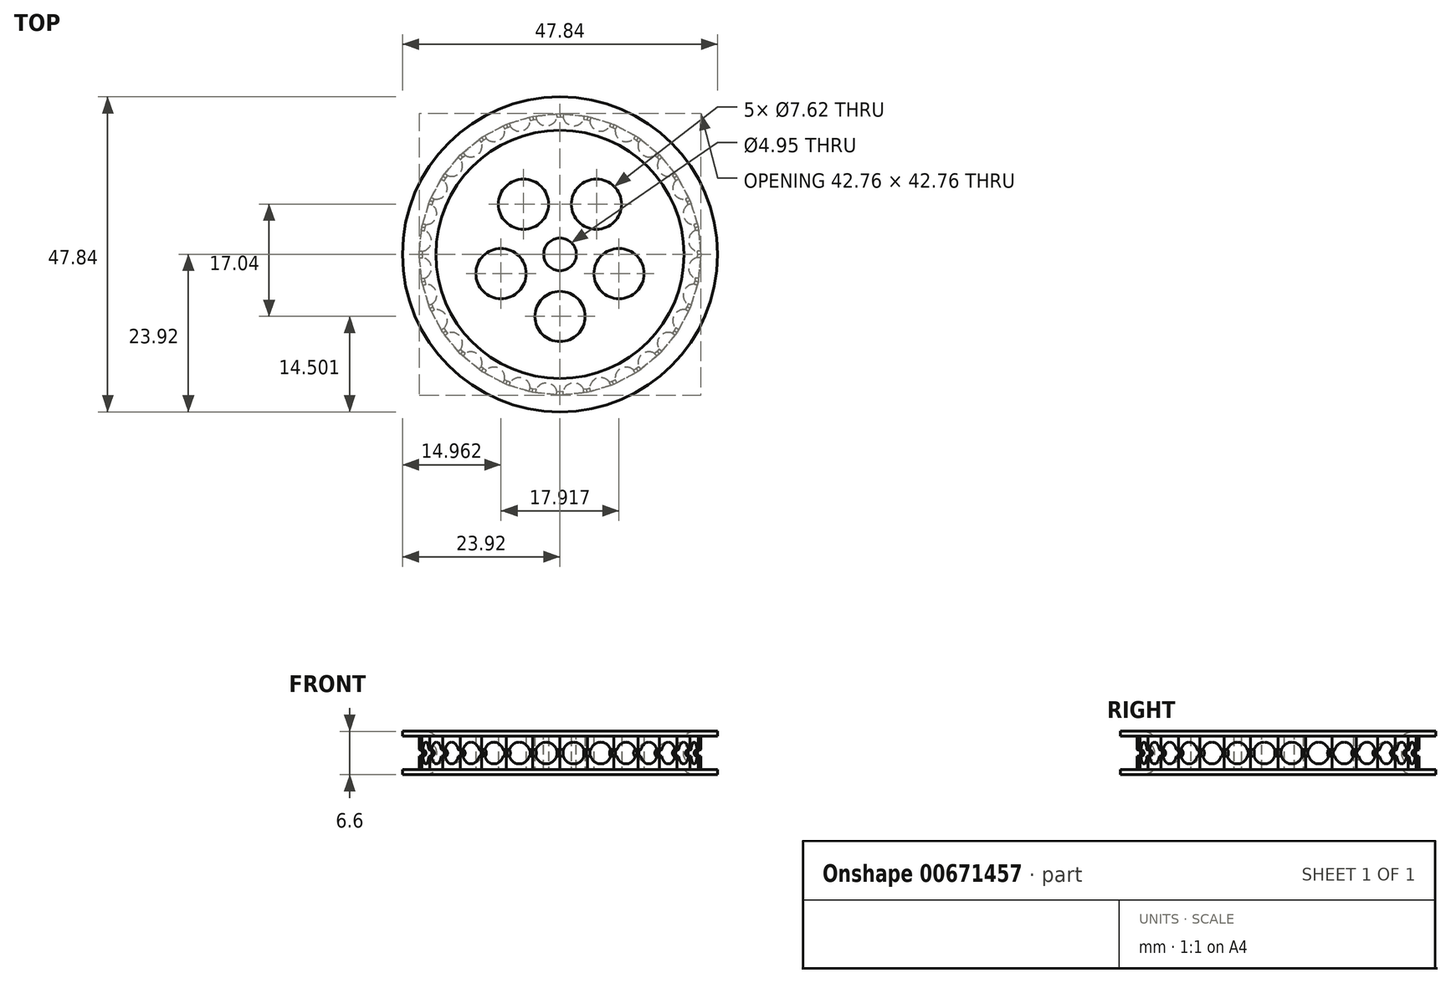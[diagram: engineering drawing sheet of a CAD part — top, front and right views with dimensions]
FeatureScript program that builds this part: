
annotation { "Feature Type Name" : "Feature", "Feature Type Description" : "" }
export const myFeature = defineFeature(function(context is Context, id is Id, definition is map)
    precondition{}
    {
        {
            var Q0;
            Q0=qCreatedBy(makeId("Top.planeOp"),FACE);
            var sketch = newSketch(context, id + "F0", { "sketchPlane" : qUnion([Q0])});
            skCircle(sketch, "E0.cCircle", {"center": v(0, 0) * mm, "radius": 21.38 * mm, "construction": true});
            skLineSegment(sketch, "E0.0", {"start": v(-21.38, 0) * mm, "end": v(-20.97, 4.17) * mm});
            skLineSegment(sketch, "E0.1", {"start": v(-20.97, 4.17) * mm, "end": v(-19.75, 8.18) * mm});
            skLineSegment(sketch, "E0.2", {"start": v(-19.75, 8.18) * mm, "end": v(-17.78, 11.88) * mm});
            skLineSegment(sketch, "E0.3", {"start": v(-17.78, 11.88) * mm, "end": v(-15.12, 15.12) * mm});
            skLineSegment(sketch, "E0.4", {"start": v(-15.12, 15.12) * mm, "end": v(-11.88, 17.78) * mm});
            skLineSegment(sketch, "E0.5", {"start": v(-11.88, 17.78) * mm, "end": v(-8.18, 19.75) * mm});
            skLineSegment(sketch, "E0.6", {"start": v(-8.18, 19.75) * mm, "end": v(-4.17, 20.97) * mm});
            skLineSegment(sketch, "E0.7", {"start": v(-4.17, 20.97) * mm, "end": v(0, 21.38) * mm});
            skLineSegment(sketch, "E0.8", {"start": v(0, 21.38) * mm, "end": v(4.17, 20.97) * mm});
            skLineSegment(sketch, "E0.9", {"start": v(4.17, 20.97) * mm, "end": v(8.18, 19.75) * mm});
            skLineSegment(sketch, "E0.10", {"start": v(8.18, 19.75) * mm, "end": v(11.88, 17.78) * mm});
            skLineSegment(sketch, "E0.11", {"start": v(11.88, 17.78) * mm, "end": v(15.12, 15.12) * mm});
            skLineSegment(sketch, "E0.12", {"start": v(15.12, 15.12) * mm, "end": v(17.78, 11.88) * mm});
            skLineSegment(sketch, "E0.13", {"start": v(17.78, 11.88) * mm, "end": v(19.75, 8.18) * mm});
            skLineSegment(sketch, "E0.14", {"start": v(19.75, 8.18) * mm, "end": v(20.97, 4.17) * mm});
            skLineSegment(sketch, "E0.15", {"start": v(20.97, 4.17) * mm, "end": v(21.38, 0) * mm});
            skLineSegment(sketch, "E0.16", {"start": v(21.38, 0) * mm, "end": v(20.97, -4.17) * mm});
            skLineSegment(sketch, "E0.17", {"start": v(20.97, -4.17) * mm, "end": v(19.75, -8.18) * mm});
            skLineSegment(sketch, "E0.18", {"start": v(19.75, -8.18) * mm, "end": v(17.78, -11.88) * mm});
            skLineSegment(sketch, "E0.19", {"start": v(17.78, -11.88) * mm, "end": v(15.12, -15.12) * mm});
            skLineSegment(sketch, "E0.20", {"start": v(15.12, -15.12) * mm, "end": v(11.88, -17.78) * mm});
            skLineSegment(sketch, "E0.21", {"start": v(11.88, -17.78) * mm, "end": v(8.18, -19.75) * mm});
            skLineSegment(sketch, "E0.22", {"start": v(8.18, -19.75) * mm, "end": v(4.17, -20.97) * mm});
            skLineSegment(sketch, "E0.23", {"start": v(4.17, -20.97) * mm, "end": v(0, -21.38) * mm});
            skLineSegment(sketch, "E0.24", {"start": v(0, -21.38) * mm, "end": v(-4.17, -20.97) * mm});
            skLineSegment(sketch, "E0.25", {"start": v(-4.17, -20.97) * mm, "end": v(-8.18, -19.75) * mm});
            skLineSegment(sketch, "E0.26", {"start": v(-8.18, -19.75) * mm, "end": v(-11.88, -17.78) * mm});
            skLineSegment(sketch, "E0.27", {"start": v(-11.88, -17.78) * mm, "end": v(-15.12, -15.12) * mm});
            skLineSegment(sketch, "E0.28", {"start": v(-15.12, -15.12) * mm, "end": v(-17.78, -11.88) * mm});
            skLineSegment(sketch, "E0.29", {"start": v(-17.78, -11.88) * mm, "end": v(-19.75, -8.18) * mm});
            skLineSegment(sketch, "E0.30", {"start": v(-19.75, -8.18) * mm, "end": v(-20.97, -4.17) * mm});
            skLineSegment(sketch, "E0.31", {"start": v(-20.97, -4.17) * mm, "end": v(-21.38, 0) * mm});
            skSolve(sketch);
        }
        {
            var Q0;
            Q0 = qSketchRegion(id + "F0", true);
            extrude(context, id + "F1", {"entities" : qUnion([Q0]), "endBound" : BoundingType.SYMMETRIC, "depth" : 5.08 * mm, "offsetDistance" : 25.4 * mm});
        }
        {
            var Q0;
            Q0=makeQuery(id+"F1.opExtrude","SWEPT_FACE",FACE,{"disambiguationData":[OSD([sQuery(id+"F0.wireOp",EDGE,"E0.28")])]});
            var sketch = newSketch(context, id + "F2", { "sketchPlane" : qUnion([Q0])});
            skLineSegment(sketch, "E1", {"start": v(2.1, 0) * mm, "end": v(-2.1, 0) * mm});
            skLineSegment(sketch, "E2", {"start": v(-2.1, 0) * mm, "end": v(-2.1, -0.5) * mm});
            skArc(sketch, "E3", {"start": v(-1.57, -0.5) * mm, "mid": v(0, -1.65) * mm, "end": v(1.57, -0.5) * mm});
            skLineSegment(sketch, "E4", {"start": v(-2.1, -0.5) * mm, "end": v(-1.57, -0.5) * mm});
            skPoint(sketch, "E5.orphan", {"position": v(-1.65, 0) * mm});
            skPoint(sketch, "E6.orphan", {"position": v(1.65, 0) * mm});
            skLineSegment(sketch, "E7", {"start": v(1.57, -0.5) * mm, "end": v(2.1, -0.5) * mm});
            skLineSegment(sketch, "E8", {"start": v(2.1, -0.5) * mm, "end": v(2.1, 0) * mm});
            skSolve(sketch);
        }
        {
            var Q0;
            Q0 = qSketchRegion(id + "F2", true);
            var Q1;
            Q1=sQuery(id+"F2.wireOp",EDGE,"E1");
            revolve(context, id + "F3", {"operationType" : NewBodyOperationType.REMOVE, "entities" : qUnion([Q0]), "axis" : qUnion([Q1]), "revolveType" : RevolveType.FULL, "oppositeDirection" : true});
        }
        {
            var Q0;
            Q0=makeQuery(id+"F1.opExtrude","SWEPT_FACE",FACE,{"disambiguationData":[OSD([sQuery(id+"F0.wireOp",EDGE,"E0.29")])]});
            var sketch = newSketch(context, id + "F4", { "sketchPlane" : qUnion([Q0])});
            skLineSegment(sketch, "E9", {"start": v(2.1, 0) * mm, "end": v(-2.1, 0) * mm});
            skPoint(sketch, "E9.startSnap0", {"position": v(-2.1, 0) * mm});
            skLineSegment(sketch, "E10", {"start": v(-2.1, 0) * mm, "end": v(-2.1, -0.5) * mm});
            skLineSegment(sketch, "E11", {"start": v(2.1, 0) * mm, "end": v(2.1, -0.5) * mm});
            skArc(sketch, "E12", {"start": v(-1.57, -0.5) * mm, "mid": v(0, -1.65) * mm, "end": v(1.57, -0.5) * mm});
            skLineSegment(sketch, "E13", {"start": v(-2.1, -0.5) * mm, "end": v(-1.57, -0.5) * mm});
            skLineSegment(sketch, "E14", {"start": v(1.57, -0.5) * mm, "end": v(2.1, -0.5) * mm});
            skPoint(sketch, "E15.orphan", {"position": v(-1.65, 0) * mm});
            skPoint(sketch, "E16.orphan", {"position": v(1.65, 0) * mm});
            skSolve(sketch);
        }
        {
            var Q0;
            Q0 = qSketchRegion(id + "F4", true);
            var Q1;
            Q1=sQuery(id+"F4.wireOp",EDGE,"E9");
            revolve(context, id + "F5", {"operationType" : NewBodyOperationType.REMOVE, "entities" : qUnion([Q0]), "axis" : qUnion([Q1]), "revolveType" : RevolveType.FULL, "oppositeDirection" : true});
        }
        {
            var Q0;
            Q0=makeQuery(id+"F1.opExtrude","SWEPT_FACE",FACE,{"disambiguationData":[OSD([sQuery(id+"F0.wireOp",EDGE,"E0.30")])]});
            var sketch = newSketch(context, id + "F6", { "sketchPlane" : qUnion([Q0])});
            skLineSegment(sketch, "E17", {"start": v(2.1, 0) * mm, "end": v(-2.1, 0) * mm});
            skLineSegment(sketch, "E18", {"start": v(-2.1, 0) * mm, "end": v(-2.1, -0.5) * mm});
            skLineSegment(sketch, "E19", {"start": v(2.1, 0) * mm, "end": v(2.1, -0.5) * mm});
            skArc(sketch, "E20", {"start": v(-1.57, -0.5) * mm, "mid": v(0, -1.65) * mm, "end": v(1.57, -0.5) * mm});
            skLineSegment(sketch, "E21", {"start": v(-2.1, -0.5) * mm, "end": v(-1.57, -0.5) * mm});
            skLineSegment(sketch, "E22", {"start": v(2.1, -0.5) * mm, "end": v(1.57, -0.5) * mm});
            skSolve(sketch);
        }
        {
            var Q0;
            Q0=makeQuery(id+"F6.imprint","IMPRINT",FACE,{"disambiguationData":[TD([[makeQuery(id+"F6.imprint","IMPRINT",EDGE,{"derivedFrom":sQuery(id+"F6.wireOp",EDGE,"E17")}),1.0]])]});
            var Q1;
            Q1=sQuery(id+"F6.wireOp",EDGE,"E17");
            revolve(context, id + "F7", {"operationType" : NewBodyOperationType.REMOVE, "entities" : qUnion([Q0]), "axis" : qUnion([Q1]), "revolveType" : RevolveType.FULL, "oppositeDirection" : true});
        }
        {
            var Q0;
            Q0=makeQuery(id+"F1.opExtrude","SWEPT_FACE",FACE,{"disambiguationData":[OSD([sQuery(id+"F0.wireOp",EDGE,"E0.31")])]});
            var sketch = newSketch(context, id + "F8", { "sketchPlane" : qUnion([Q0])});
            skLineSegment(sketch, "E23", {"start": v(2.1, 0) * mm, "end": v(-2.1, 0) * mm});
            skLineSegment(sketch, "E24", {"start": v(-2.1, -0.5) * mm, "end": v(-2.1, 0) * mm});
            skLineSegment(sketch, "E25", {"start": v(2.1, -0.5) * mm, "end": v(2.1, 0) * mm});
            skArc(sketch, "E26", {"start": v(-1.57, -0.5) * mm, "mid": v(0, -1.65) * mm, "end": v(1.57, -0.5) * mm});
            skLineSegment(sketch, "E27", {"start": v(-2.1, -0.5) * mm, "end": v(-1.57, -0.5) * mm});
            skLineSegment(sketch, "E28", {"start": v(2.1, -0.5) * mm, "end": v(1.57, -0.5) * mm});
            skSolve(sketch);
        }
        {
            var Q0;
            Q0 = qSketchRegion(id + "F8", true);
            var Q1;
            Q1=sQuery(id+"F8.wireOp",EDGE,"E23");
            revolve(context, id + "F9", {"operationType" : NewBodyOperationType.REMOVE, "entities" : qUnion([Q0]), "axis" : qUnion([Q1]), "revolveType" : RevolveType.FULL, "oppositeDirection" : true});
        }
        {
            var Q0;
            Q0=makeQuery(id+"F1.opExtrude","SWEPT_FACE",FACE,{"disambiguationData":[OSD([sQuery(id+"F0.wireOp",EDGE,"E0.0")])]});
            var sketch = newSketch(context, id + "F10", { "sketchPlane" : qUnion([Q0])});
            skLineSegment(sketch, "E29", {"start": v(2.1, 0) * mm, "end": v(-2.1, 0) * mm});
            skArc(sketch, "E30", {"start": v(-1.57, -0.5) * mm, "mid": v(0, -1.65) * mm, "end": v(1.57, -0.5) * mm});
            skLineSegment(sketch, "E31", {"start": v(2.1, -0.5) * mm, "end": v(1.57, -0.5) * mm});
            skLineSegment(sketch, "E32", {"start": v(2.1, -0.5) * mm, "end": v(2.1, 0) * mm});
            skLineSegment(sketch, "E33", {"start": v(-1.57, -0.5) * mm, "end": v(-2.1, -0.5) * mm});
            skLineSegment(sketch, "E34", {"start": v(-2.1, -0.5) * mm, "end": v(-2.1, 0) * mm});
            skSolve(sketch);
        }
        {
            var Q0;
            Q0 = qSketchRegion(id + "F10", true);
            var Q1;
            Q1=sQuery(id+"F10.wireOp",EDGE,"E29");
            revolve(context, id + "F11", {"operationType" : NewBodyOperationType.REMOVE, "entities" : qUnion([Q0]), "axis" : qUnion([Q1]), "revolveType" : RevolveType.FULL, "oppositeDirection" : true});
        }
        {
            var Q0;
            Q0=makeQuery(id+"F1.opExtrude","SWEPT_FACE",FACE,{"disambiguationData":[OSD([sQuery(id+"F0.wireOp",EDGE,"E0.1")])]});
            var sketch = newSketch(context, id + "F12", { "sketchPlane" : qUnion([Q0])});
            skLineSegment(sketch, "E35", {"start": v(2.1, 0) * mm, "end": v(-2.1, 0) * mm});
            skArc(sketch, "E36", {"start": v(-1.57, -0.5) * mm, "mid": v(0, -1.65) * mm, "end": v(1.57, -0.5) * mm});
            skLineSegment(sketch, "E37", {"start": v(2.1, -0.5) * mm, "end": v(1.57, -0.5) * mm});
            skLineSegment(sketch, "E38", {"start": v(1.57, -0.5) * mm, "end": v(2.1, -0.5) * mm});
            skLineSegment(sketch, "E39", {"start": v(2.1, 0) * mm, "end": v(2.1, -0.5) * mm});
            skLineSegment(sketch, "E40", {"start": v(-2.1, 0) * mm, "end": v(-2.1, -0.5) * mm});
            skLineSegment(sketch, "E41", {"start": v(-2.1, -0.5) * mm, "end": v(-1.57, -0.5) * mm});
            skSolve(sketch);
        }
        {
            var Q0;
            Q0 = qSketchRegion(id + "F12", true);
            var Q1;
            Q1=sQuery(id+"F12.wireOp",EDGE,"E35");
            revolve(context, id + "F13", {"operationType" : NewBodyOperationType.REMOVE, "entities" : qUnion([Q0]), "axis" : qUnion([Q1]), "revolveType" : RevolveType.FULL, "oppositeDirection" : true});
        }
        {
            var Q0;
            Q0=makeQuery(id+"F1.opExtrude","SWEPT_FACE",FACE,{"disambiguationData":[OSD([sQuery(id+"F0.wireOp",EDGE,"E0.2")])]});
            var sketch = newSketch(context, id + "F14", { "sketchPlane" : qUnion([Q0])});
            skLineSegment(sketch, "E42", {"start": v(2.1, 0) * mm, "end": v(-2.1, 0) * mm});
            skArc(sketch, "E43", {"start": v(-1.57, -0.5) * mm, "mid": v(0, -1.65) * mm, "end": v(1.57, -0.5) * mm});
            skLineSegment(sketch, "E44", {"start": v(2.1, -0.5) * mm, "end": v(1.57, -0.5) * mm});
            skLineSegment(sketch, "E45", {"start": v(-1.57, -0.5) * mm, "end": v(-2.1, -0.5) * mm});
            skLineSegment(sketch, "E46", {"start": v(-2.1, -0.5) * mm, "end": v(-2.1, 0) * mm});
            skLineSegment(sketch, "E47", {"start": v(2.1, -0.5) * mm, "end": v(2.1, 0) * mm});
            skSolve(sketch);
        }
        {
            var Q0;
            Q0 = qSketchRegion(id + "F14", true);
            var Q1;
            Q1=sQuery(id+"F14.wireOp",EDGE,"E42");
            revolve(context, id + "F15", {"operationType" : NewBodyOperationType.REMOVE, "entities" : qUnion([Q0]), "axis" : qUnion([Q1]), "revolveType" : RevolveType.FULL, "oppositeDirection" : true});
        }
        {
            var Q0;
            Q0=makeQuery(id+"F1.opExtrude","SWEPT_FACE",FACE,{"disambiguationData":[OSD([sQuery(id+"F0.wireOp",EDGE,"E0.3")])]});
            var sketch = newSketch(context, id + "F16", { "sketchPlane" : qUnion([Q0])});
            skLineSegment(sketch, "E48", {"start": v(2.1, 0) * mm, "end": v(-2.1, 0) * mm});
            skArc(sketch, "E49", {"start": v(-1.57, -0.5) * mm, "mid": v(0, -1.65) * mm, "end": v(1.57, -0.5) * mm});
            skLineSegment(sketch, "E50", {"start": v(2.1, -0.5) * mm, "end": v(1.57, -0.5) * mm});
            skLineSegment(sketch, "E51", {"start": v(-1.57, -0.5) * mm, "end": v(-2.1, -0.5) * mm});
            skLineSegment(sketch, "E52", {"start": v(-2.1, -0.5) * mm, "end": v(-2.1, 0) * mm});
            skLineSegment(sketch, "E53", {"start": v(2.1, -0.5) * mm, "end": v(2.1, 0) * mm});
            skSolve(sketch);
        }
        {
            var Q0;
            Q0 = qSketchRegion(id + "F16", true);
            var Q1;
            Q1=sQuery(id+"F16.wireOp",EDGE,"E48");
            revolve(context, id + "F17", {"operationType" : NewBodyOperationType.REMOVE, "entities" : qUnion([Q0]), "axis" : qUnion([Q1]), "revolveType" : RevolveType.FULL, "oppositeDirection" : true});
        }
        {
            var Q0;
            Q0=makeQuery(id+"F1.opExtrude","SWEPT_FACE",FACE,{"disambiguationData":[OSD([sQuery(id+"F0.wireOp",EDGE,"E0.4")])]});
            var sketch = newSketch(context, id + "F18", { "sketchPlane" : qUnion([Q0])});
            skLineSegment(sketch, "E54", {"start": v(2.1, 0) * mm, "end": v(-2.1, 0) * mm});
            skArc(sketch, "E55", {"start": v(-1.57, -0.5) * mm, "mid": v(0, -1.65) * mm, "end": v(1.57, -0.5) * mm});
            skLineSegment(sketch, "E56", {"start": v(2.1, -0.5) * mm, "end": v(1.57, -0.5) * mm});
            skLineSegment(sketch, "E57", {"start": v(2.1, 0) * mm, "end": v(2.1, -0.5) * mm});
            skLineSegment(sketch, "E58", {"start": v(-2.1, 0) * mm, "end": v(-2.1, -0.5) * mm});
            skLineSegment(sketch, "E59", {"start": v(-2.1, -0.5) * mm, "end": v(-1.57, -0.5) * mm});
            skSolve(sketch);
        }
        {
            var Q0;
            Q0 = qSketchRegion(id + "F18", true);
            var Q1;
            Q1=sQuery(id+"F18.wireOp",EDGE,"E54");
            revolve(context, id + "F19", {"operationType" : NewBodyOperationType.REMOVE, "entities" : qUnion([Q0]), "axis" : qUnion([Q1]), "revolveType" : RevolveType.FULL, "oppositeDirection" : true});
        }
        {
            var Q0;
            Q0=makeQuery(id+"F1.opExtrude","SWEPT_FACE",FACE,{"disambiguationData":[OSD([sQuery(id+"F0.wireOp",EDGE,"E0.5")])]});
            var sketch = newSketch(context, id + "F20", { "sketchPlane" : qUnion([Q0])});
            skLineSegment(sketch, "E60", {"start": v(2.1, 0) * mm, "end": v(-2.1, 0) * mm});
            skLineSegment(sketch, "E61", {"start": v(-2.1, 0) * mm, "end": v(-2.1, -0.5) * mm});
            skLineSegment(sketch, "E62", {"start": v(2.1, 0) * mm, "end": v(2.1, -0.5) * mm});
            skLineSegment(sketch, "E63", {"start": v(-2.1, -0.5) * mm, "end": v(-1.57, -0.5) * mm});
            skArc(sketch, "E64", {"start": v(-1.57, -0.5) * mm, "mid": v(0, -1.65) * mm, "end": v(1.57, -0.5) * mm});
            skLineSegment(sketch, "E65.trimOffspring", {"start": v(1.57, -0.5) * mm, "end": v(2.1, -0.5) * mm});
            skSolve(sketch);
        }
        {
            var Q0;
            Q0 = qSketchRegion(id + "F20", true);
            var Q1;
            Q1=sQuery(id+"F20.wireOp",EDGE,"E60");
            revolve(context, id + "F21", {"operationType" : NewBodyOperationType.REMOVE, "entities" : qUnion([Q0]), "axis" : qUnion([Q1]), "revolveType" : RevolveType.FULL, "oppositeDirection" : true});
        }
        {
            var Q0;
            Q0=makeQuery(id+"F1.opExtrude","SWEPT_FACE",FACE,{"disambiguationData":[OSD([sQuery(id+"F0.wireOp",EDGE,"E0.6")])]});
            var sketch = newSketch(context, id + "F22", { "sketchPlane" : qUnion([Q0])});
            skLineSegment(sketch, "E66", {"start": v(2.1, 0) * mm, "end": v(-2.1, 0) * mm});
            skLineSegment(sketch, "E67", {"start": v(-2.1, 0) * mm, "end": v(-2.1, -0.5) * mm});
            skLineSegment(sketch, "E68", {"start": v(-2.1, -0.5) * mm, "end": v(-1.57, -0.5) * mm});
            skLineSegment(sketch, "E69", {"start": v(2.1, -0.5) * mm, "end": v(2.1, 0) * mm});
            skArc(sketch, "E70", {"start": v(-1.57, -0.5) * mm, "mid": v(0, -1.65) * mm, "end": v(1.57, -0.5) * mm});
            skLineSegment(sketch, "E71.trimOffspring", {"start": v(1.57, -0.5) * mm, "end": v(2.1, -0.5) * mm});
            skSolve(sketch);
        }
        {
            var Q0;
            Q0 = qSketchRegion(id + "F22", true);
            var Q1;
            Q1=sQuery(id+"F22.wireOp",EDGE,"E66");
            revolve(context, id + "F23", {"operationType" : NewBodyOperationType.REMOVE, "entities" : qUnion([Q0]), "axis" : qUnion([Q1]), "revolveType" : RevolveType.FULL, "oppositeDirection" : true});
        }
        {
            var Q0;
            Q0=makeQuery(id+"F1.opExtrude","SWEPT_FACE",FACE,{"disambiguationData":[OSD([sQuery(id+"F0.wireOp",EDGE,"E0.7")])]});
            var sketch = newSketch(context, id + "F24", { "sketchPlane" : qUnion([Q0])});
            skLineSegment(sketch, "E72", {"start": v(2.1, 0) * mm, "end": v(-2.1, 0) * mm});
            skLineSegment(sketch, "E73", {"start": v(-2.1, 0) * mm, "end": v(-2.1, -0.5) * mm});
            skLineSegment(sketch, "E74", {"start": v(-2.1, -0.5) * mm, "end": v(-1.57, -0.5) * mm});
            skLineSegment(sketch, "E75", {"start": v(2.1, -0.5) * mm, "end": v(2.1, 0) * mm});
            skArc(sketch, "E76", {"start": v(-1.57, -0.5) * mm, "mid": v(0, -1.65) * mm, "end": v(1.57, -0.5) * mm});
            skLineSegment(sketch, "E77.trimOffspring", {"start": v(1.57, -0.5) * mm, "end": v(2.1, -0.5) * mm});
            skSolve(sketch);
        }
        {
            var Q0;
            Q0 = qSketchRegion(id + "F24", true);
            var Q1;
            Q1=sQuery(id+"F24.wireOp",EDGE,"E72");
            revolve(context, id + "F25", {"operationType" : NewBodyOperationType.REMOVE, "entities" : qUnion([Q0]), "axis" : qUnion([Q1]), "revolveType" : RevolveType.FULL, "oppositeDirection" : true});
        }
        {
            var Q0;
            Q0=makeQuery(id+"F1.opExtrude","SWEPT_FACE",FACE,{"disambiguationData":[OSD([sQuery(id+"F0.wireOp",EDGE,"E0.8")])]});
            var sketch = newSketch(context, id + "F26", { "sketchPlane" : qUnion([Q0])});
            skLineSegment(sketch, "E78", {"start": v(2.1, 0) * mm, "end": v(-2.1, 0) * mm});
            skLineSegment(sketch, "E79", {"start": v(-2.1, 0) * mm, "end": v(-2.1, -0.5) * mm});
            skLineSegment(sketch, "E80", {"start": v(-2.1, -0.5) * mm, "end": v(-1.57, -0.5) * mm});
            skLineSegment(sketch, "E81", {"start": v(2.1, -0.5) * mm, "end": v(2.1, 0) * mm});
            skArc(sketch, "E82", {"start": v(-1.57, -0.5) * mm, "mid": v(0, -1.65) * mm, "end": v(1.57, -0.5) * mm});
            skLineSegment(sketch, "E83.trimOffspring", {"start": v(1.57, -0.5) * mm, "end": v(2.1, -0.5) * mm});
            skSolve(sketch);
        }
        {
            var Q0;
            Q0 = qSketchRegion(id + "F26", true);
            var Q1;
            Q1=sQuery(id+"F26.wireOp",EDGE,"E78");
            revolve(context, id + "F27", {"operationType" : NewBodyOperationType.REMOVE, "entities" : qUnion([Q0]), "axis" : qUnion([Q1]), "revolveType" : RevolveType.FULL, "oppositeDirection" : true});
        }
        {
            var Q0;
            Q0=makeQuery(id+"F1.opExtrude","SWEPT_FACE",FACE,{"disambiguationData":[OSD([sQuery(id+"F0.wireOp",EDGE,"E0.9")])]});
            var sketch = newSketch(context, id + "F28", { "sketchPlane" : qUnion([Q0])});
            skLineSegment(sketch, "E84", {"start": v(2.1, 0) * mm, "end": v(-2.1, 0) * mm});
            skLineSegment(sketch, "E85", {"start": v(-2.1, 0) * mm, "end": v(-2.1, -0.5) * mm});
            skLineSegment(sketch, "E86", {"start": v(2.1, -0.5) * mm, "end": v(1.57, -0.5) * mm});
            skLineSegment(sketch, "E87", {"start": v(2.1, -0.5) * mm, "end": v(2.1, 0) * mm});
            skArc(sketch, "E88", {"start": v(-1.57, -0.5) * mm, "mid": v(0, -1.65) * mm, "end": v(1.57, -0.5) * mm});
            skLineSegment(sketch, "E89.trimOffspring", {"start": v(-1.57, -0.5) * mm, "end": v(-2.1, -0.5) * mm});
            skSolve(sketch);
        }
        {
            var Q0;
            Q0 = qSketchRegion(id + "F28", true);
            var Q1;
            Q1=sQuery(id+"F28.wireOp",EDGE,"E84");
            revolve(context, id + "F29", {"operationType" : NewBodyOperationType.REMOVE, "entities" : qUnion([Q0]), "axis" : qUnion([Q1]), "revolveType" : RevolveType.FULL, "oppositeDirection" : true});
        }
        {
            var Q0;
            Q0=makeQuery(id+"F1.opExtrude","SWEPT_FACE",FACE,{"disambiguationData":[OSD([sQuery(id+"F0.wireOp",EDGE,"E0.10")])]});
            var sketch = newSketch(context, id + "F30", { "sketchPlane" : qUnion([Q0])});
            skLineSegment(sketch, "E90", {"start": v(2.1, 0) * mm, "end": v(-2.1, 0) * mm});
            skLineSegment(sketch, "E91", {"start": v(-2.1, 0) * mm, "end": v(-2.1, -0.5) * mm});
            skLineSegment(sketch, "E92", {"start": v(-2.1, -0.5) * mm, "end": v(-1.57, -0.5) * mm});
            skLineSegment(sketch, "E93", {"start": v(2.1, 0) * mm, "end": v(2.1, -0.5) * mm});
            skArc(sketch, "E94", {"start": v(-1.57, -0.5) * mm, "mid": v(0, -1.65) * mm, "end": v(1.57, -0.5) * mm});
            skLineSegment(sketch, "E95.trimOffspring", {"start": v(1.57, -0.5) * mm, "end": v(2.1, -0.5) * mm});
            skSolve(sketch);
        }
        {
            var Q0;
            Q0 = qSketchRegion(id + "F30", true);
            var Q1;
            Q1=sQuery(id+"F30.wireOp",EDGE,"E90");
            revolve(context, id + "F31", {"operationType" : NewBodyOperationType.REMOVE, "entities" : qUnion([Q0]), "axis" : qUnion([Q1]), "revolveType" : RevolveType.FULL, "oppositeDirection" : true});
        }
        {
            var Q0;
            Q0=makeQuery(id+"F1.opExtrude","SWEPT_FACE",FACE,{"disambiguationData":[OSD([sQuery(id+"F0.wireOp",EDGE,"E0.11")])]});
            var sketch = newSketch(context, id + "F32", { "sketchPlane" : qUnion([Q0])});
            skLineSegment(sketch, "E96", {"start": v(2.1, 0) * mm, "end": v(-2.1, 0) * mm});
            skLineSegment(sketch, "E97", {"start": v(-2.1, 0) * mm, "end": v(-2.1, -0.5) * mm});
            skLineSegment(sketch, "E98", {"start": v(-2.1, -0.5) * mm, "end": v(-1.57, -0.5) * mm});
            skLineSegment(sketch, "E99", {"start": v(2.1, -0.5) * mm, "end": v(2.1, 0) * mm});
            skArc(sketch, "E100", {"start": v(-1.57, -0.5) * mm, "mid": v(0, -1.65) * mm, "end": v(1.57, -0.5) * mm});
            skLineSegment(sketch, "E101.trimOffspring", {"start": v(1.57, -0.5) * mm, "end": v(2.1, -0.5) * mm});
            skSolve(sketch);
        }
        {
            var Q0;
            Q0 = qSketchRegion(id + "F32", true);
            var Q1;
            Q1=sQuery(id+"F32.wireOp",EDGE,"E96");
            revolve(context, id + "F33", {"operationType" : NewBodyOperationType.REMOVE, "entities" : qUnion([Q0]), "axis" : qUnion([Q1]), "revolveType" : RevolveType.FULL, "oppositeDirection" : true});
        }
        {
            var Q0;
            Q0=makeQuery(id+"F1.opExtrude","SWEPT_FACE",FACE,{"disambiguationData":[OSD([sQuery(id+"F0.wireOp",EDGE,"E0.12")])]});
            var sketch = newSketch(context, id + "F34", { "sketchPlane" : qUnion([Q0])});
            skLineSegment(sketch, "E102", {"start": v(2.1, 0) * mm, "end": v(-2.1, 0) * mm});
            skLineSegment(sketch, "E103", {"start": v(-2.1, 0) * mm, "end": v(-2.1, -0.5) * mm});
            skLineSegment(sketch, "E104", {"start": v(-2.1, -0.5) * mm, "end": v(-1.57, -0.5) * mm});
            skArc(sketch, "E105", {"start": v(-1.57, -0.5) * mm, "mid": v(0, -1.65) * mm, "end": v(1.57, -0.5) * mm});
            skLineSegment(sketch, "E106.trimOffspring", {"start": v(1.57, -0.5) * mm, "end": v(2.1, -0.5) * mm});
            skSolve(sketch);
        }
        {
            var Q0;
            {var subQ0=sQuery(id+"F34.wireOp",EDGE,"E102");Q0=makeQuery(id+"F34.imprint","IMPRINT",FACE,{"disambiguationData":[TD([[makeQuery(id+"F34.imprint","IMPRINT",EDGE,{"derivedFrom":subQ0}),1.0]])]});}
            var Q1;
            Q1=sQuery(id+"F34.wireOp",EDGE,"E102");
            revolve(context, id + "F35", {"operationType" : NewBodyOperationType.REMOVE, "entities" : qUnion([Q0]), "axis" : qUnion([Q1]), "revolveType" : RevolveType.FULL, "oppositeDirection" : true});
        }
        {
            var Q0;
            Q0=makeQuery(id+"F1.opExtrude","SWEPT_FACE",FACE,{"disambiguationData":[OSD([sQuery(id+"F0.wireOp",EDGE,"E0.13")])]});
            var sketch = newSketch(context, id + "F36", { "sketchPlane" : qUnion([Q0])});
            skLineSegment(sketch, "E107", {"start": v(2.1, 0) * mm, "end": v(-2.1, 0) * mm});
            skLineSegment(sketch, "E108", {"start": v(-2.1, -0.5) * mm, "end": v(-2.1, 0) * mm});
            skLineSegment(sketch, "E109", {"start": v(-2.1, -0.5) * mm, "end": v(-1.57, -0.5) * mm});
            skLineSegment(sketch, "E110", {"start": v(2.1, 0) * mm, "end": v(2.1, -0.5) * mm});
            skArc(sketch, "E111", {"start": v(-1.57, -0.5) * mm, "mid": v(0, -1.65) * mm, "end": v(1.57, -0.5) * mm});
            skLineSegment(sketch, "E112.trimOffspring", {"start": v(1.57, -0.5) * mm, "end": v(2.1, -0.5) * mm});
            skSolve(sketch);
        }
        {
            var Q0;
            Q0 = qSketchRegion(id + "F36", true);
            var Q1;
            Q1=sQuery(id+"F36.wireOp",EDGE,"E107");
            revolve(context, id + "F37", {"operationType" : NewBodyOperationType.REMOVE, "entities" : qUnion([Q0]), "axis" : qUnion([Q1]), "revolveType" : RevolveType.FULL, "oppositeDirection" : true});
        }
        {
            var Q0;
            Q0=makeQuery(id+"F1.opExtrude","SWEPT_FACE",FACE,{"disambiguationData":[OSD([sQuery(id+"F0.wireOp",EDGE,"E0.14")])]});
            var sketch = newSketch(context, id + "F38", { "sketchPlane" : qUnion([Q0])});
            skLineSegment(sketch, "E113", {"start": v(2.1, 0) * mm, "end": v(-2.1, 0) * mm});
            skLineSegment(sketch, "E114", {"start": v(-2.1, 0) * mm, "end": v(-2.1, -0.5) * mm});
            skLineSegment(sketch, "E115", {"start": v(-2.1, -0.5) * mm, "end": v(-1.57, -0.5) * mm});
            skLineSegment(sketch, "E116", {"start": v(2.1, -0.5) * mm, "end": v(2.1, 0) * mm});
            skArc(sketch, "E117", {"start": v(-1.57, -0.5) * mm, "mid": v(0, -1.65) * mm, "end": v(1.57, -0.5) * mm});
            skLineSegment(sketch, "E118.trimOffspring", {"start": v(1.57, -0.5) * mm, "end": v(2.1, -0.5) * mm});
            skSolve(sketch);
        }
        {
            var Q0;
            Q0 = qSketchRegion(id + "F38", true);
            var Q1;
            Q1=sQuery(id+"F38.wireOp",EDGE,"E113");
            revolve(context, id + "F39", {"operationType" : NewBodyOperationType.REMOVE, "entities" : qUnion([Q0]), "axis" : qUnion([Q1]), "revolveType" : RevolveType.FULL, "oppositeDirection" : true});
        }
        {
            var Q0;
            Q0=makeQuery(id+"F1.opExtrude","SWEPT_FACE",FACE,{"disambiguationData":[OSD([sQuery(id+"F0.wireOp",EDGE,"E0.15")])]});
            var sketch = newSketch(context, id + "F40", { "sketchPlane" : qUnion([Q0])});
            skLineSegment(sketch, "E119", {"start": v(2.1, 0) * mm, "end": v(-2.1, 0) * mm});
            skLineSegment(sketch, "E120", {"start": v(-2.1, 0) * mm, "end": v(-2.1, -0.5) * mm});
            skLineSegment(sketch, "E121", {"start": v(-2.1, -0.5) * mm, "end": v(-1.57, -0.5) * mm});
            skLineSegment(sketch, "E122", {"start": v(2.1, 0) * mm, "end": v(2.1, -0.5) * mm});
            skArc(sketch, "E123", {"start": v(-1.57, -0.5) * mm, "mid": v(0, -1.65) * mm, "end": v(1.57, -0.5) * mm});
            skLineSegment(sketch, "E124.trimOffspring", {"start": v(1.57, -0.5) * mm, "end": v(2.1, -0.5) * mm});
            skSolve(sketch);
        }
        {
            var Q0;
            Q0 = qSketchRegion(id + "F40", true);
            var Q1;
            Q1=sQuery(id+"F40.wireOp",EDGE,"E119");
            revolve(context, id + "F41", {"operationType" : NewBodyOperationType.REMOVE, "entities" : qUnion([Q0]), "axis" : qUnion([Q1]), "revolveType" : RevolveType.FULL, "oppositeDirection" : true});
        }
        {
            var Q0;
            Q0=makeQuery(id+"F1.opExtrude","SWEPT_FACE",FACE,{"disambiguationData":[OSD([sQuery(id+"F0.wireOp",EDGE,"E0.16")])]});
            var sketch = newSketch(context, id + "F42", { "sketchPlane" : qUnion([Q0])});
            skLineSegment(sketch, "E125", {"start": v(2.1, 0) * mm, "end": v(-2.1, 0) * mm});
            skLineSegment(sketch, "E126", {"start": v(-2.1, 0) * mm, "end": v(-2.1, -0.5) * mm});
            skLineSegment(sketch, "E127", {"start": v(2.1, 0) * mm, "end": v(2.1, -0.5) * mm});
            skLineSegment(sketch, "E128", {"start": v(2.1, -0.5) * mm, "end": v(1.57, -0.5) * mm});
            skArc(sketch, "E129", {"start": v(-1.57, -0.5) * mm, "mid": v(0, -1.65) * mm, "end": v(1.57, -0.5) * mm});
            skLineSegment(sketch, "E130.trimOffspring", {"start": v(-1.57, -0.5) * mm, "end": v(-2.1, -0.5) * mm});
            skSolve(sketch);
        }
        {
            var Q0;
            Q0 = qSketchRegion(id + "F42", true);
            var Q1;
            Q1=sQuery(id+"F42.wireOp",EDGE,"E125");
            revolve(context, id + "F43", {"operationType" : NewBodyOperationType.REMOVE, "entities" : qUnion([Q0]), "axis" : qUnion([Q1]), "revolveType" : RevolveType.FULL, "oppositeDirection" : true});
        }
        {
            var Q0;
            Q0=makeQuery(id+"F1.opExtrude","SWEPT_FACE",FACE,{"disambiguationData":[OSD([sQuery(id+"F0.wireOp",EDGE,"E0.17")])]});
            var sketch = newSketch(context, id + "F44", { "sketchPlane" : qUnion([Q0])});
            skLineSegment(sketch, "E131", {"start": v(2.1, 0) * mm, "end": v(-2.1, 0) * mm});
            skLineSegment(sketch, "E132", {"start": v(-2.1, -0.5) * mm, "end": v(-2.1, 0) * mm});
            skLineSegment(sketch, "E133", {"start": v(-2.1, -0.5) * mm, "end": v(-1.57, -0.5) * mm});
            skLineSegment(sketch, "E134", {"start": v(2.1, -0.5) * mm, "end": v(2.1, 0) * mm});
            skArc(sketch, "E135", {"start": v(-1.57, -0.5) * mm, "mid": v(0, -1.65) * mm, "end": v(1.57, -0.5) * mm});
            skLineSegment(sketch, "E136.trimOffspring", {"start": v(1.57, -0.5) * mm, "end": v(2.1, -0.5) * mm});
            skSolve(sketch);
        }
        {
            var Q0;
            Q0 = qSketchRegion(id + "F44", true);
            var Q1;
            Q1=sQuery(id+"F44.wireOp",EDGE,"E131");
            revolve(context, id + "F45", {"operationType" : NewBodyOperationType.REMOVE, "entities" : qUnion([Q0]), "axis" : qUnion([Q1]), "revolveType" : RevolveType.FULL, "oppositeDirection" : true});
        }
        {
            var Q0;
            Q0=makeQuery(id+"F1.opExtrude","SWEPT_FACE",FACE,{"disambiguationData":[OSD([sQuery(id+"F0.wireOp",EDGE,"E0.18")])]});
            var sketch = newSketch(context, id + "F46", { "sketchPlane" : qUnion([Q0])});
            skLineSegment(sketch, "E137", {"start": v(2.1, 0) * mm, "end": v(-2.1, 0) * mm});
            skLineSegment(sketch, "E138", {"start": v(-2.1, 0) * mm, "end": v(-2.1, -0.5) * mm});
            skLineSegment(sketch, "E139", {"start": v(-2.1, -0.5) * mm, "end": v(-1.57, -0.5) * mm});
            skLineSegment(sketch, "E140", {"start": v(2.1, -0.5) * mm, "end": v(2.1, 0) * mm});
            skArc(sketch, "E141", {"start": v(-1.57, -0.5) * mm, "mid": v(0, -1.65) * mm, "end": v(1.57, -0.5) * mm});
            skLineSegment(sketch, "E142.trimOffspring", {"start": v(1.57, -0.5) * mm, "end": v(2.1, -0.5) * mm});
            skSolve(sketch);
        }
        {
            var Q0;
            Q0 = qSketchRegion(id + "F46", true);
            var Q1;
            Q1=sQuery(id+"F46.wireOp",EDGE,"E137");
            revolve(context, id + "F47", {"operationType" : NewBodyOperationType.REMOVE, "entities" : qUnion([Q0]), "axis" : qUnion([Q1]), "revolveType" : RevolveType.FULL, "oppositeDirection" : true});
        }
        {
            var Q0;
            Q0=makeQuery(id+"F1.opExtrude","SWEPT_FACE",FACE,{"disambiguationData":[OSD([sQuery(id+"F0.wireOp",EDGE,"E0.19")])]});
            var sketch = newSketch(context, id + "F48", { "sketchPlane" : qUnion([Q0])});
            skLineSegment(sketch, "E143", {"start": v(2.1, 0) * mm, "end": v(-2.1, 0) * mm});
            skLineSegment(sketch, "E144", {"start": v(-2.1, 0) * mm, "end": v(-2.1, -0.5) * mm});
            skLineSegment(sketch, "E145", {"start": v(-2.1, -0.5) * mm, "end": v(-1.57, -0.5) * mm});
            skLineSegment(sketch, "E146", {"start": v(2.1, -0.5) * mm, "end": v(2.1, 0) * mm});
            skArc(sketch, "E147", {"start": v(-1.57, -0.5) * mm, "mid": v(0, -1.65) * mm, "end": v(1.57, -0.5) * mm});
            skLineSegment(sketch, "E148.trimOffspring", {"start": v(1.57, -0.5) * mm, "end": v(2.1, -0.5) * mm});
            skSolve(sketch);
        }
        {
            var Q0;
            Q0 = qSketchRegion(id + "F48", true);
            var Q1;
            Q1=sQuery(id+"F48.wireOp",EDGE,"E143");
            revolve(context, id + "F49", {"operationType" : NewBodyOperationType.REMOVE, "entities" : qUnion([Q0]), "axis" : qUnion([Q1]), "revolveType" : RevolveType.FULL, "oppositeDirection" : true});
        }
        {
            var Q0;
            Q0=makeQuery(id+"F1.opExtrude","SWEPT_FACE",FACE,{"disambiguationData":[OSD([sQuery(id+"F0.wireOp",EDGE,"E0.20")])]});
            var sketch = newSketch(context, id + "F50", { "sketchPlane" : qUnion([Q0])});
            skLineSegment(sketch, "E149", {"start": v(2.1, 0) * mm, "end": v(-2.1, 0) * mm});
            skLineSegment(sketch, "E150", {"start": v(-2.1, 0) * mm, "end": v(-2.1, -0.5) * mm});
            skLineSegment(sketch, "E151", {"start": v(-2.1, -0.5) * mm, "end": v(-1.57, -0.5) * mm});
            skLineSegment(sketch, "E152", {"start": v(2.1, -0.5) * mm, "end": v(2.1, 0) * mm});
            skArc(sketch, "E153", {"start": v(-1.57, -0.5) * mm, "mid": v(0, -1.65) * mm, "end": v(1.57, -0.5) * mm});
            skLineSegment(sketch, "E154.trimOffspring", {"start": v(1.57, -0.5) * mm, "end": v(2.1, -0.5) * mm});
            skSolve(sketch);
        }
        {
            var Q0;
            Q0 = qSketchRegion(id + "F50", true);
            var Q1;
            Q1=sQuery(id+"F50.wireOp",EDGE,"E149");
            revolve(context, id + "F51", {"operationType" : NewBodyOperationType.REMOVE, "entities" : qUnion([Q0]), "axis" : qUnion([Q1]), "revolveType" : RevolveType.FULL, "oppositeDirection" : true});
        }
        {
            var Q0;
            Q0=makeQuery(id+"F1.opExtrude","SWEPT_FACE",FACE,{"disambiguationData":[OSD([sQuery(id+"F0.wireOp",EDGE,"E0.21")])]});
            var sketch = newSketch(context, id + "F52", { "sketchPlane" : qUnion([Q0])});
            skLineSegment(sketch, "E155", {"start": v(2.1, 0) * mm, "end": v(-2.1, 0) * mm});
            skLineSegment(sketch, "E156", {"start": v(-2.1, 0) * mm, "end": v(-2.1, -0.5) * mm});
            skLineSegment(sketch, "E157", {"start": v(-2.1, -0.5) * mm, "end": v(-1.57, -0.5) * mm});
            skLineSegment(sketch, "E158", {"start": v(2.1, -0.5) * mm, "end": v(2.1, 0) * mm});
            skArc(sketch, "E159", {"start": v(-1.57, -0.5) * mm, "mid": v(0, -1.65) * mm, "end": v(1.57, -0.5) * mm});
            skLineSegment(sketch, "E160.trimOffspring", {"start": v(1.57, -0.5) * mm, "end": v(2.1, -0.5) * mm});
            skSolve(sketch);
        }
        {
            var Q0;
            Q0 = qSketchRegion(id + "F52", true);
            var Q1;
            Q1=sQuery(id+"F52.wireOp",EDGE,"E155");
            revolve(context, id + "F53", {"operationType" : NewBodyOperationType.REMOVE, "entities" : qUnion([Q0]), "axis" : qUnion([Q1]), "revolveType" : RevolveType.FULL, "oppositeDirection" : true});
        }
        {
            var Q0;
            Q0=makeQuery(id+"F1.opExtrude","SWEPT_FACE",FACE,{"disambiguationData":[OSD([sQuery(id+"F0.wireOp",EDGE,"E0.22")])]});
            var sketch = newSketch(context, id + "F54", { "sketchPlane" : qUnion([Q0])});
            skLineSegment(sketch, "E161", {"start": v(2.1, 0) * mm, "end": v(-2.1, 0) * mm});
            skLineSegment(sketch, "E162", {"start": v(-2.1, 0) * mm, "end": v(-2.1, -0.5) * mm});
            skLineSegment(sketch, "E163", {"start": v(-2.1, -0.5) * mm, "end": v(-1.57, -0.5) * mm});
            skLineSegment(sketch, "E164", {"start": v(2.1, -0.5) * mm, "end": v(2.1, 0) * mm});
            skArc(sketch, "E165", {"start": v(-1.57, -0.5) * mm, "mid": v(0, -1.65) * mm, "end": v(1.57, -0.5) * mm});
            skLineSegment(sketch, "E166.trimOffspring", {"start": v(1.57, -0.5) * mm, "end": v(2.1, -0.5) * mm});
            skSolve(sketch);
        }
        {
            var Q0;
            Q0 = qSketchRegion(id + "F54", true);
            var Q1;
            Q1=sQuery(id+"F54.wireOp",EDGE,"E161");
            revolve(context, id + "F55", {"operationType" : NewBodyOperationType.REMOVE, "entities" : qUnion([Q0]), "axis" : qUnion([Q1]), "revolveType" : RevolveType.FULL, "oppositeDirection" : true});
        }
        {
            var Q0;
            Q0=makeQuery(id+"F1.opExtrude","SWEPT_FACE",FACE,{"disambiguationData":[OSD([sQuery(id+"F0.wireOp",EDGE,"E0.23")])]});
            var sketch = newSketch(context, id + "F56", { "sketchPlane" : qUnion([Q0])});
            skLineSegment(sketch, "E167", {"start": v(2.1, 0) * mm, "end": v(-2.1, 0) * mm});
            skLineSegment(sketch, "E168", {"start": v(-2.1, 0) * mm, "end": v(-2.1, -0.5) * mm});
            skLineSegment(sketch, "E169", {"start": v(2.1, -0.5) * mm, "end": v(1.57, -0.5) * mm});
            skLineSegment(sketch, "E170", {"start": v(2.1, -0.5) * mm, "end": v(2.1, 0) * mm});
            skArc(sketch, "E171", {"start": v(-1.57, -0.5) * mm, "mid": v(0, -1.65) * mm, "end": v(1.57, -0.5) * mm});
            skLineSegment(sketch, "E172.trimOffspring", {"start": v(-1.57, -0.5) * mm, "end": v(-2.1, -0.5) * mm});
            skSolve(sketch);
        }
        {
            var Q0;
            Q0 = qSketchRegion(id + "F56", true);
            var Q1;
            Q1=sQuery(id+"F56.wireOp",EDGE,"E167");
            revolve(context, id + "F57", {"operationType" : NewBodyOperationType.REMOVE, "entities" : qUnion([Q0]), "axis" : qUnion([Q1]), "revolveType" : RevolveType.FULL, "oppositeDirection" : true});
        }
        {
            var Q0;
            Q0=makeQuery(id+"F1.opExtrude","SWEPT_FACE",FACE,{"disambiguationData":[OSD([sQuery(id+"F0.wireOp",EDGE,"E0.24")])]});
            var sketch = newSketch(context, id + "F58", { "sketchPlane" : qUnion([Q0])});
            skLineSegment(sketch, "E173", {"start": v(2.1, 0) * mm, "end": v(-2.1, 0) * mm});
            skLineSegment(sketch, "E174", {"start": v(-2.1, 0) * mm, "end": v(-2.1, -0.5) * mm});
            skLineSegment(sketch, "E175", {"start": v(-2.1, -0.5) * mm, "end": v(-1.57, -0.5) * mm});
            skLineSegment(sketch, "E176", {"start": v(2.1, -0.5) * mm, "end": v(2.1, 0) * mm});
            skArc(sketch, "E177", {"start": v(-1.57, -0.5) * mm, "mid": v(0, -1.65) * mm, "end": v(1.57, -0.5) * mm});
            skLineSegment(sketch, "E178.trimOffspring", {"start": v(1.57, -0.5) * mm, "end": v(2.1, -0.5) * mm});
            skSolve(sketch);
        }
        {
            var Q0;
            Q0 = qSketchRegion(id + "F58", true);
            var Q1;
            Q1=sQuery(id+"F58.wireOp",EDGE,"E173");
            revolve(context, id + "F59", {"operationType" : NewBodyOperationType.REMOVE, "entities" : qUnion([Q0]), "axis" : qUnion([Q1]), "revolveType" : RevolveType.FULL, "oppositeDirection" : true});
        }
        {
            var Q0;
            Q0=makeQuery(id+"F1.opExtrude","CAP_FACE",FACE,{"disambiguationData":[OSD([sQuery(id+"F0.wireOp",EDGE,"E0.0"),sQuery(id+"F0.wireOp",EDGE,"E0.1"),sQuery(id+"F0.wireOp",EDGE,"E0.2"),sQuery(id+"F0.wireOp",EDGE,"E0.3"),sQuery(id+"F0.wireOp",EDGE,"E0.4"),sQuery(id+"F0.wireOp",EDGE,"E0.5"),sQuery(id+"F0.wireOp",EDGE,"E0.6"),sQuery(id+"F0.wireOp",EDGE,"E0.7"),sQuery(id+"F0.wireOp",EDGE,"E0.8"),sQuery(id+"F0.wireOp",EDGE,"E0.9"),sQuery(id+"F0.wireOp",EDGE,"E0.10"),sQuery(id+"F0.wireOp",EDGE,"E0.11"),sQuery(id+"F0.wireOp",EDGE,"E0.12"),sQuery(id+"F0.wireOp",EDGE,"E0.13"),sQuery(id+"F0.wireOp",EDGE,"E0.14"),sQuery(id+"F0.wireOp",EDGE,"E0.15"),sQuery(id+"F0.wireOp",EDGE,"E0.16"),sQuery(id+"F0.wireOp",EDGE,"E0.17"),sQuery(id+"F0.wireOp",EDGE,"E0.18"),sQuery(id+"F0.wireOp",EDGE,"E0.19"),sQuery(id+"F0.wireOp",EDGE,"E0.20"),sQuery(id+"F0.wireOp",EDGE,"E0.21"),sQuery(id+"F0.wireOp",EDGE,"E0.22"),sQuery(id+"F0.wireOp",EDGE,"E0.23"),sQuery(id+"F0.wireOp",EDGE,"E0.24"),sQuery(id+"F0.wireOp",EDGE,"E0.25"),sQuery(id+"F0.wireOp",EDGE,"E0.26"),sQuery(id+"F0.wireOp",EDGE,"E0.27"),sQuery(id+"F0.wireOp",EDGE,"E0.28"),sQuery(id+"F0.wireOp",EDGE,"E0.29"),sQuery(id+"F0.wireOp",EDGE,"E0.30"),sQuery(id+"F0.wireOp",EDGE,"E0.31")])],"isStart":false});
            var sketch = newSketch(context, id + "F60", { "sketchPlane" : qUnion([Q0])});
            skCircle(sketch, "E179", {"center": v(0, 0) * mm, "radius": 2.48 * mm});
            skSolve(sketch);
        }
        {
            var Q0;
            Q0 = qSketchRegion(id + "F60", true);
            extrude(context, id + "F61", {"entities" : qUnion([Q0]), "operationType" : NewBodyOperationType.REMOVE, "endBound" : BoundingType.THROUGH_ALL, "oppositeDirection" : true, "depth" : 25.4 * mm, "offsetDistance" : 25.4 * mm});
        }
        {
            var Q0;
            Q0=makeQuery(id+"F1.opExtrude","SWEPT_FACE",FACE,{"disambiguationData":[OSD([sQuery(id+"F0.wireOp",EDGE,"E0.25")])]});
            var sketch = newSketch(context, id + "F62", { "sketchPlane" : qUnion([Q0])});
            skLineSegment(sketch, "E180", {"start": v(2.1, 0) * mm, "end": v(-2.1, 0) * mm});
            skLineSegment(sketch, "E181", {"start": v(2.1, 0) * mm, "end": v(2.1, -0.5) * mm});
            skLineSegment(sketch, "E182", {"start": v(2.1, -0.5) * mm, "end": v(1.57, -0.5) * mm});
            skLineSegment(sketch, "E183", {"start": v(-2.1, -0.5) * mm, "end": v(-2.1, 0) * mm});
            skArc(sketch, "E184", {"start": v(-1.57, -0.5) * mm, "mid": v(0, -1.65) * mm, "end": v(1.57, -0.5) * mm});
            skLineSegment(sketch, "E185.trimOffspring", {"start": v(-1.57, -0.5) * mm, "end": v(-2.1, -0.5) * mm});
            skSolve(sketch);
        }
        {
            var Q0;
            Q0 = qSketchRegion(id + "F62", true);
            var Q1;
            Q1=sQuery(id+"F0.wireOp",EDGE,"E0.25");
            revolve(context, id + "F63", {"operationType" : NewBodyOperationType.REMOVE, "entities" : qUnion([Q0]), "axis" : qUnion([Q1]), "revolveType" : RevolveType.FULL, "oppositeDirection" : true});
        }
        {
            var Q0;
            Q0=makeQuery(id+"F1.opExtrude","SWEPT_FACE",FACE,{"disambiguationData":[OSD([sQuery(id+"F0.wireOp",EDGE,"E0.26")])]});
            var sketch = newSketch(context, id + "F64", { "sketchPlane" : qUnion([Q0])});
            skLineSegment(sketch, "E186", {"start": v(2.1, 0) * mm, "end": v(-2.1, 0) * mm});
            skLineSegment(sketch, "E187", {"start": v(-2.1, 0) * mm, "end": v(-2.1, -0.5) * mm});
            skLineSegment(sketch, "E188", {"start": v(-2.1, -0.5) * mm, "end": v(-1.57, -0.5) * mm});
            skLineSegment(sketch, "E189", {"start": v(2.1, -0.5) * mm, "end": v(2.1, 0) * mm});
            skArc(sketch, "E190", {"start": v(-1.57, -0.5) * mm, "mid": v(0, -1.65) * mm, "end": v(1.57, -0.5) * mm});
            skLineSegment(sketch, "E191.trimOffspring", {"start": v(1.57, -0.5) * mm, "end": v(2.1, -0.5) * mm});
            skSolve(sketch);
        }
        {
            var Q0;
            Q0 = qSketchRegion(id + "F64", true);
            var Q1;
            Q1=sQuery(id+"F0.wireOp",EDGE,"E0.26");
            revolve(context, id + "F65", {"operationType" : NewBodyOperationType.REMOVE, "entities" : qUnion([Q0]), "axis" : qUnion([Q1]), "revolveType" : RevolveType.FULL, "oppositeDirection" : true});
        }
        {
            var Q0;
            Q0=makeQuery(id+"F1.opExtrude","SWEPT_FACE",FACE,{"disambiguationData":[OSD([sQuery(id+"F0.wireOp",EDGE,"E0.27")])]});
            var sketch = newSketch(context, id + "F66", { "sketchPlane" : qUnion([Q0])});
            skLineSegment(sketch, "E192", {"start": v(2.1, 0) * mm, "end": v(-2.1, 0) * mm});
            skLineSegment(sketch, "E193", {"start": v(-2.1, -0.5) * mm, "end": v(-2.1, 0) * mm});
            skLineSegment(sketch, "E194", {"start": v(-2.1, -0.5) * mm, "end": v(-1.57, -0.5) * mm});
            skLineSegment(sketch, "E195", {"start": v(2.1, -0.5) * mm, "end": v(2.1, 0) * mm});
            skArc(sketch, "E196", {"start": v(-1.57, -0.5) * mm, "mid": v(0, -1.65) * mm, "end": v(1.57, -0.5) * mm});
            skLineSegment(sketch, "E197.trimOffspring", {"start": v(1.57, -0.5) * mm, "end": v(2.1, -0.5) * mm});
            skSolve(sketch);
        }
        {
            var Q0;
            Q0 = qSketchRegion(id + "F66", true);
            var Q1;
            Q1=sQuery(id+"F0.wireOp",EDGE,"E0.27");
            revolve(context, id + "F67", {"operationType" : NewBodyOperationType.REMOVE, "entities" : qUnion([Q0]), "axis" : qUnion([Q1]), "revolveType" : RevolveType.FULL, "oppositeDirection" : true});
        }
        {
            var Q0;
            Q0=makeQuery(id+"F1.opExtrude","CAP_FACE",FACE,{"disambiguationData":[OSD([sQuery(id+"F0.wireOp",EDGE,"E0.0"),sQuery(id+"F0.wireOp",EDGE,"E0.1"),sQuery(id+"F0.wireOp",EDGE,"E0.2"),sQuery(id+"F0.wireOp",EDGE,"E0.3"),sQuery(id+"F0.wireOp",EDGE,"E0.4"),sQuery(id+"F0.wireOp",EDGE,"E0.5"),sQuery(id+"F0.wireOp",EDGE,"E0.6"),sQuery(id+"F0.wireOp",EDGE,"E0.7"),sQuery(id+"F0.wireOp",EDGE,"E0.8"),sQuery(id+"F0.wireOp",EDGE,"E0.9"),sQuery(id+"F0.wireOp",EDGE,"E0.10"),sQuery(id+"F0.wireOp",EDGE,"E0.11"),sQuery(id+"F0.wireOp",EDGE,"E0.12"),sQuery(id+"F0.wireOp",EDGE,"E0.13"),sQuery(id+"F0.wireOp",EDGE,"E0.14"),sQuery(id+"F0.wireOp",EDGE,"E0.15"),sQuery(id+"F0.wireOp",EDGE,"E0.16"),sQuery(id+"F0.wireOp",EDGE,"E0.17"),sQuery(id+"F0.wireOp",EDGE,"E0.18"),sQuery(id+"F0.wireOp",EDGE,"E0.19"),sQuery(id+"F0.wireOp",EDGE,"E0.20"),sQuery(id+"F0.wireOp",EDGE,"E0.21"),sQuery(id+"F0.wireOp",EDGE,"E0.22"),sQuery(id+"F0.wireOp",EDGE,"E0.23"),sQuery(id+"F0.wireOp",EDGE,"E0.24"),sQuery(id+"F0.wireOp",EDGE,"E0.25"),sQuery(id+"F0.wireOp",EDGE,"E0.26"),sQuery(id+"F0.wireOp",EDGE,"E0.27"),sQuery(id+"F0.wireOp",EDGE,"E0.28"),sQuery(id+"F0.wireOp",EDGE,"E0.29"),sQuery(id+"F0.wireOp",EDGE,"E0.30"),sQuery(id+"F0.wireOp",EDGE,"E0.31")])],"isStart":true});
            var sketch = newSketch(context, id + "F68", { "sketchPlane" : qUnion([Q0])});
            skCircle(sketch, "E198", {"center": v(0, 0) * mm, "radius": 23.92 * mm});
            skCircle(sketch, "E199", {"center": v(0, 0) * mm, "radius": 18.84 * mm});
            skSolve(sketch);
        }
        {
            var Q0;
            Q0=makeQuery(id+"F68.imprint","IMPRINT",FACE,{"disambiguationData":[TD([[makeQuery(id+"F68.imprint","IMPRINT",EDGE,{"derivedFrom":sQuery(id+"F68.wireOp",EDGE,"E198")}),1.0]])]});
            var Q1;
            {var subQ15=sQuery(id+"F0.wireOp",EDGE,"E0.0");Q1=makeQuery(id+"F68.imprint","IMPRINT",FACE,{"disambiguationData":[TD([[makeQuery(id+"F68.imprint","IMPRINT",EDGE,{"derivedFrom":makeQuery(id+"F1.opExtrude","CAP_EDGE",EDGE,{"disambiguationData":[OSD([subQ15])],"isStart":true})}),1.0]])]});}
            extrude(context, id + "F69", {"entities" : qUnion([Q0, Q1]), "operationType" : NewBodyOperationType.ADD, "depth" : 0.76 * mm, "offsetDistance" : 25.4 * mm});
        }
        {
            var Q0;
            Q0=makeQuery(id+"F1.opExtrude","CAP_FACE",FACE,{"disambiguationData":[OSD([sQuery(id+"F0.wireOp",EDGE,"E0.0"),sQuery(id+"F0.wireOp",EDGE,"E0.1"),sQuery(id+"F0.wireOp",EDGE,"E0.2"),sQuery(id+"F0.wireOp",EDGE,"E0.3"),sQuery(id+"F0.wireOp",EDGE,"E0.4"),sQuery(id+"F0.wireOp",EDGE,"E0.5"),sQuery(id+"F0.wireOp",EDGE,"E0.6"),sQuery(id+"F0.wireOp",EDGE,"E0.7"),sQuery(id+"F0.wireOp",EDGE,"E0.8"),sQuery(id+"F0.wireOp",EDGE,"E0.9"),sQuery(id+"F0.wireOp",EDGE,"E0.10"),sQuery(id+"F0.wireOp",EDGE,"E0.11"),sQuery(id+"F0.wireOp",EDGE,"E0.12"),sQuery(id+"F0.wireOp",EDGE,"E0.13"),sQuery(id+"F0.wireOp",EDGE,"E0.14"),sQuery(id+"F0.wireOp",EDGE,"E0.15"),sQuery(id+"F0.wireOp",EDGE,"E0.16"),sQuery(id+"F0.wireOp",EDGE,"E0.17"),sQuery(id+"F0.wireOp",EDGE,"E0.18"),sQuery(id+"F0.wireOp",EDGE,"E0.19"),sQuery(id+"F0.wireOp",EDGE,"E0.20"),sQuery(id+"F0.wireOp",EDGE,"E0.21"),sQuery(id+"F0.wireOp",EDGE,"E0.22"),sQuery(id+"F0.wireOp",EDGE,"E0.23"),sQuery(id+"F0.wireOp",EDGE,"E0.24"),sQuery(id+"F0.wireOp",EDGE,"E0.25"),sQuery(id+"F0.wireOp",EDGE,"E0.26"),sQuery(id+"F0.wireOp",EDGE,"E0.27"),sQuery(id+"F0.wireOp",EDGE,"E0.28"),sQuery(id+"F0.wireOp",EDGE,"E0.29"),sQuery(id+"F0.wireOp",EDGE,"E0.30"),sQuery(id+"F0.wireOp",EDGE,"E0.31")])],"isStart":false});
            var sketch = newSketch(context, id + "F70", { "sketchPlane" : qUnion([Q0])});
            skCircle(sketch, "E200", {"center": v(0, 0) * mm, "radius": 23.92 * mm});
            skCircle(sketch, "E201", {"center": v(0, 0) * mm, "radius": 18.84 * mm});
            skSolve(sketch);
        }
        {
            var Q0;
            Q0=makeQuery(id+"F70.imprint","IMPRINT",FACE,{"disambiguationData":[TD([[makeQuery(id+"F70.imprint","IMPRINT",EDGE,{"derivedFrom":sQuery(id+"F70.wireOp",EDGE,"E200")}),1.0]])]});
            var Q1;
            Q1=makeQuery(id+"F70.imprint","IMPRINT",FACE,{"disambiguationData":[TD([[makeQuery(id+"F70.imprint","IMPRINT",EDGE,{"derivedFrom":sQuery(id+"F70.wireOp",EDGE,"E201")}),-1.0]])]});
            extrude(context, id + "F71", {"entities" : qUnion([Q0, Q1]), "operationType" : NewBodyOperationType.ADD, "depth" : 0.76 * mm, "offsetDistance" : 25.4 * mm});
        }
        {
            var Q0;
            Q0=makeQuery(id+"F71.opExtrude","CAP_EDGE",EDGE,{"disambiguationData":[OSD([sQuery(id+"F70.wireOp",EDGE,"E201")])],"isStart":false});
            var Q1;
            Q1=makeQuery(id+"F69.opExtrude","CAP_EDGE",EDGE,{"disambiguationData":[OSD([sQuery(id+"F68.wireOp",EDGE,"E199")])],"isStart":false});
            fillet(context, id + "F72", {"entities" : qUnion([Q0, Q1]), "radius" : 2.54 * mm, "tangentPropagation" : true, "allowEdgeOverflow" : false});
        }
        {
            var Q0;
            Q0=makeQuery(id+"F1.opExtrude","CAP_FACE",FACE,{"disambiguationData":[OSD([sQuery(id+"F0.wireOp",EDGE,"E0.0"),sQuery(id+"F0.wireOp",EDGE,"E0.1"),sQuery(id+"F0.wireOp",EDGE,"E0.2"),sQuery(id+"F0.wireOp",EDGE,"E0.3"),sQuery(id+"F0.wireOp",EDGE,"E0.4"),sQuery(id+"F0.wireOp",EDGE,"E0.5"),sQuery(id+"F0.wireOp",EDGE,"E0.6"),sQuery(id+"F0.wireOp",EDGE,"E0.7"),sQuery(id+"F0.wireOp",EDGE,"E0.8"),sQuery(id+"F0.wireOp",EDGE,"E0.9"),sQuery(id+"F0.wireOp",EDGE,"E0.10"),sQuery(id+"F0.wireOp",EDGE,"E0.11"),sQuery(id+"F0.wireOp",EDGE,"E0.12"),sQuery(id+"F0.wireOp",EDGE,"E0.13"),sQuery(id+"F0.wireOp",EDGE,"E0.14"),sQuery(id+"F0.wireOp",EDGE,"E0.15"),sQuery(id+"F0.wireOp",EDGE,"E0.16"),sQuery(id+"F0.wireOp",EDGE,"E0.17"),sQuery(id+"F0.wireOp",EDGE,"E0.18"),sQuery(id+"F0.wireOp",EDGE,"E0.19"),sQuery(id+"F0.wireOp",EDGE,"E0.20"),sQuery(id+"F0.wireOp",EDGE,"E0.21"),sQuery(id+"F0.wireOp",EDGE,"E0.22"),sQuery(id+"F0.wireOp",EDGE,"E0.23"),sQuery(id+"F0.wireOp",EDGE,"E0.24"),sQuery(id+"F0.wireOp",EDGE,"E0.25"),sQuery(id+"F0.wireOp",EDGE,"E0.26"),sQuery(id+"F0.wireOp",EDGE,"E0.27"),sQuery(id+"F0.wireOp",EDGE,"E0.28"),sQuery(id+"F0.wireOp",EDGE,"E0.29"),sQuery(id+"F0.wireOp",EDGE,"E0.30"),sQuery(id+"F0.wireOp",EDGE,"E0.31")])],"isStart":true});
            var sketch = newSketch(context, id + "F73", { "sketchPlane" : qUnion([Q0])});
            skCircle(sketch, "E202", {"center": v(0, 9.42) * mm, "radius": 3.81 * mm});
            skLineSegment(sketch, "E203", {"start": v(0, 0) * mm, "end": v(0, 18.84) * mm, "construction": true});
            skCircle(sketch, "E204.1.0", {"center": v(-8.96, 2.91) * mm, "radius": 3.81 * mm});
            skCircle(sketch, "E204.2.0", {"center": v(-5.54, -7.62) * mm, "radius": 3.81 * mm});
            skCircle(sketch, "E204.3.0", {"center": v(5.54, -7.62) * mm, "radius": 3.81 * mm});
            skCircle(sketch, "E204.4.0", {"center": v(8.96, 2.91) * mm, "radius": 3.81 * mm});
            skPoint(sketch, "E204.center", {"position": v(0, 0) * mm});
            skSolve(sketch);
        }
        {
            var Q0;
            Q0=makeQuery(id+"F73.imprint","IMPRINT",FACE,{"disambiguationData":[TD([[makeQuery(id+"F73.imprint","IMPRINT",EDGE,{"derivedFrom":sQuery(id+"F73.wireOp",EDGE,"E204.1.0")}),1.0]])]});
            var Q1;
            Q1=makeQuery(id+"F73.imprint","IMPRINT",FACE,{"disambiguationData":[TD([[makeQuery(id+"F73.imprint","IMPRINT",EDGE,{"derivedFrom":sQuery(id+"F73.wireOp",EDGE,"E202")}),1.0]])]});
            var Q2;
            Q2=makeQuery(id+"F73.imprint","IMPRINT",FACE,{"disambiguationData":[TD([[makeQuery(id+"F73.imprint","IMPRINT",EDGE,{"derivedFrom":sQuery(id+"F73.wireOp",EDGE,"E204.4.0")}),1.0]])]});
            var Q3;
            Q3=makeQuery(id+"F73.imprint","IMPRINT",FACE,{"disambiguationData":[TD([[makeQuery(id+"F73.imprint","IMPRINT",EDGE,{"derivedFrom":sQuery(id+"F73.wireOp",EDGE,"E204.3.0")}),1.0]])]});
            var Q4;
            Q4=makeQuery(id+"F73.imprint","IMPRINT",FACE,{"disambiguationData":[TD([[makeQuery(id+"F73.imprint","IMPRINT",EDGE,{"derivedFrom":sQuery(id+"F73.wireOp",EDGE,"E204.2.0")}),1.0]])]});
            extrude(context, id + "F74", {"entities" : qUnion([Q0, Q1, Q2, Q3, Q4]), "operationType" : NewBodyOperationType.REMOVE, "endBound" : BoundingType.THROUGH_ALL, "oppositeDirection" : true, "depth" : 25.4 * mm, "offsetDistance" : 25.4 * mm});
        }
    });
